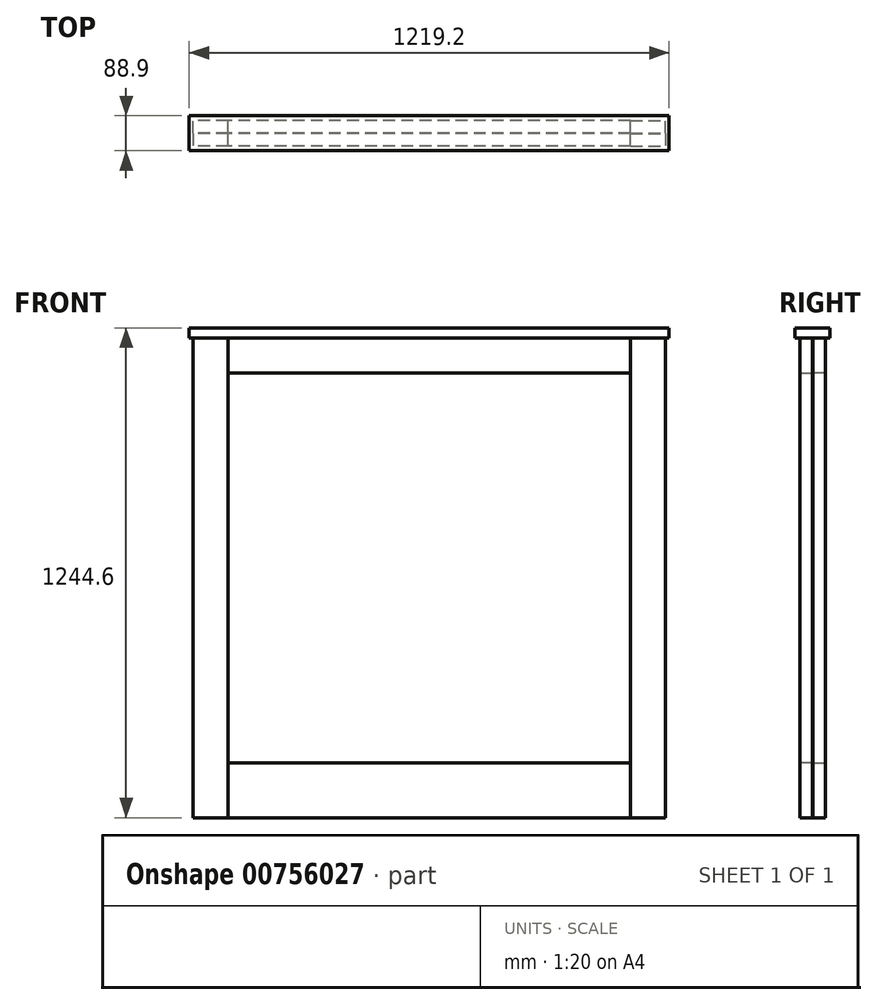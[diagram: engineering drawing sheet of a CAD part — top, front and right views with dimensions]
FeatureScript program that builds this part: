
annotation { "Feature Type Name" : "Feature", "Feature Type Description" : "" }
export const myFeature = defineFeature(function(context is Context, id is Id, definition is map)
    precondition{}
    {
        {
            var Q0;
            Q0=qCreatedBy(makeId("Top.planeOp"),FACE);
            var sketch = newSketch(context, id + "F0", { "sketchPlane" : qUnion([Q0])});
            skLineSegment(sketch, "E0.bottom", {"start": v(511.18, -0.8) * mm, "end": v(600.08, -0.8) * mm});
            skLineSegment(sketch, "E0.top", {"start": v(511.18, -32.54) * mm, "end": v(600.08, -32.54) * mm});
            skLineSegment(sketch, "E0.left", {"start": v(511.18, -0.8) * mm, "end": v(511.18, -32.54) * mm});
            skLineSegment(sketch, "E0.right", {"start": v(600.08, -0.8) * mm, "end": v(600.08, -32.54) * mm});
            skLineSegment(sketch, "E1.bottom", {"start": v(-511.18, -0.8) * mm, "end": v(-600.08, -0.8) * mm});
            skLineSegment(sketch, "E1.top", {"start": v(-511.18, -32.54) * mm, "end": v(-600.08, -32.54) * mm});
            skLineSegment(sketch, "E1.left", {"start": v(-511.18, -0.8) * mm, "end": v(-511.18, -32.54) * mm});
            skLineSegment(sketch, "E1.right", {"start": v(-600.08, -0.8) * mm, "end": v(-600.08, -32.54) * mm});
            skSolve(sketch);
        }
        {
            var Q0;
            Q0=makeQuery(id+"F0.imprint","IMPRINT",FACE,{"disambiguationData":[TD([[makeQuery(id+"F0.imprint","IMPRINT",EDGE,{"derivedFrom":sQuery(id+"F0.wireOp",EDGE,"E1.bottom")}),1.0]])]});
            var Q1;
            Q1=makeQuery(id+"F0.imprint","IMPRINT",FACE,{"disambiguationData":[TD([[makeQuery(id+"F0.imprint","IMPRINT",EDGE,{"derivedFrom":sQuery(id+"F0.wireOp",EDGE,"E0.bottom")}),-1.0]])]});
            extrude(context, id + "F1", {"entities" : qUnion([Q0, Q1]), "depth" : 1219.2 * mm, "offsetDistance" : 25.4 * mm});
        }
        {
            var Q0;
            Q0=qCreatedBy(makeId("Right.planeOp"),FACE);
            var sketch = newSketch(context, id + "F2", { "sketchPlane" : qUnion([Q0])});
            skLineSegment(sketch, "E2.bottom", {"start": v(-32.54, 1219.2) * mm, "end": v(-0.8, 1219.2) * mm});
            skLineSegment(sketch, "E2.top", {"start": v(-32.54, 1130.3) * mm, "end": v(-0.8, 1130.3) * mm});
            skLineSegment(sketch, "E2.left", {"start": v(-32.54, 1219.2) * mm, "end": v(-32.54, 1130.3) * mm});
            skLineSegment(sketch, "E2.right", {"start": v(-0.8, 1219.2) * mm, "end": v(-0.8, 1130.3) * mm});
            skLineSegment(sketch, "E3.bottom", {"start": v(-0.8, 139.7) * mm, "end": v(-32.54, 139.7) * mm});
            skLineSegment(sketch, "E3.top", {"start": v(-0.8, 0) * mm, "end": v(-32.54, 0) * mm});
            skLineSegment(sketch, "E3.left", {"start": v(-0.8, 139.7) * mm, "end": v(-0.8, 0) * mm});
            skLineSegment(sketch, "E3.right", {"start": v(-32.54, 139.7) * mm, "end": v(-32.54, 0) * mm});
            skPoint(sketch, "E4.oppositeSnap0", {"position": v(-16.67, 0) * mm});
            skSolve(sketch);
        }
        {
            var Q0;
            Q0=makeQuery(id+"F2.imprint","IMPRINT",FACE,{"disambiguationData":[TD([[makeQuery(id+"F2.imprint","IMPRINT",EDGE,{"derivedFrom":sQuery(id+"F2.wireOp",EDGE,"E3.bottom")}),1.0]])]});
            var Q1;
            Q1=makeQuery(id+"F2.imprint","IMPRINT",FACE,{"disambiguationData":[TD([[makeQuery(id+"F2.imprint","IMPRINT",EDGE,{"derivedFrom":sQuery(id+"F2.wireOp",EDGE,"E2.bottom")}),-1.0]])]});
            var Q2;
            Q2=makeQuery(id+"F1.opExtrude","SWEPT_FACE",FACE,{"disambiguationData":[OSD([sQuery(id+"F0.wireOp",EDGE,"E0.left")])]});
            var Q3;
            Q3=makeQuery(id+"F1.opExtrude","SWEPT_FACE",FACE,{"disambiguationData":[OSD([sQuery(id+"F0.wireOp",EDGE,"E1.left")])]});
            extrude(context, id + "F3", {"entities" : qUnion([Q0, Q1]), "endBound" : BoundingType.UP_TO_SURFACE, "depth" : 25.4 * mm, "endBoundEntityFace" : qUnion([Q2]), "offsetDistance" : 25.4 * mm, "hasSecondDirection" : true, "secondDirectionBound" : SecondDirectionBoundingType.UP_TO_SURFACE, "secondDirectionOppositeDirection" : true, "secondDirectionDepth" : 25.4 * mm, "secondDirectionBoundEntityFace" : qUnion([Q3])});
        }
        {
            var Q0;
            Q0=makeQuery(id+"F1.opExtrude","SWEPT_BODY",BODY,{"disambiguationData":[OSD([sQuery(id+"F0.wireOp",EDGE,"E0.bottom"),sQuery(id+"F0.wireOp",EDGE,"E0.top"),sQuery(id+"F0.wireOp",EDGE,"E0.left"),sQuery(id+"F0.wireOp",EDGE,"E0.right")])]});
            var Q1;
            Q1=makeQuery(id+"F3.opExtrude","SWEPT_BODY",BODY,{"disambiguationData":[OSD([sQuery(id+"F2.wireOp",EDGE,"E3.bottom"),sQuery(id+"F2.wireOp",EDGE,"E3.top"),sQuery(id+"F2.wireOp",EDGE,"E3.left"),sQuery(id+"F2.wireOp",EDGE,"E3.right")])]});
            var Q2;
            Q2=makeQuery(id+"F3.opExtrude","SWEPT_BODY",BODY,{"disambiguationData":[OSD([sQuery(id+"F2.wireOp",EDGE,"E2.bottom"),sQuery(id+"F2.wireOp",EDGE,"E2.top"),sQuery(id+"F2.wireOp",EDGE,"E2.left"),sQuery(id+"F2.wireOp",EDGE,"E2.right")])]});
            var Q3;
            Q3=makeQuery(id+"F1.opExtrude","SWEPT_BODY",BODY,{"disambiguationData":[OSD([sQuery(id+"F0.wireOp",EDGE,"E1.bottom"),sQuery(id+"F0.wireOp",EDGE,"E1.top"),sQuery(id+"F0.wireOp",EDGE,"E1.left"),sQuery(id+"F0.wireOp",EDGE,"E1.right")])]});
            var Q4;
            Q4=qCreatedBy(makeId("Front.planeOp"),FACE);
            mirror(context, id + "F4", {"entities" : qUnion([Q0, Q1, Q2, Q3]), "mirrorPlane" : qUnion([Q4])});
        }
        {
            var Q0;
            Q0=qCreatedBy(makeId("Right.planeOp"),FACE);
            var sketch = newSketch(context, id + "F5", { "sketchPlane" : qUnion([Q0])});
            skLineSegment(sketch, "E5.bottom", {"start": v(-44.45, 1244.6) * mm, "end": v(44.45, 1244.6) * mm});
            skLineSegment(sketch, "E5.top", {"start": v(-44.45, 1219.2) * mm, "end": v(44.45, 1219.2) * mm});
            skLineSegment(sketch, "E5.left", {"start": v(-44.45, 1244.6) * mm, "end": v(-44.45, 1219.2) * mm});
            skLineSegment(sketch, "E5.right", {"start": v(44.45, 1244.6) * mm, "end": v(44.45, 1219.2) * mm});
            skSolve(sketch);
        }
        {
            var Q0;
            Q0=makeQuery(id+"F5.imprint","IMPRINT",FACE,{"disambiguationData":[TD([[makeQuery(id+"F5.imprint","IMPRINT",EDGE,{"derivedFrom":sQuery(id+"F5.wireOp",EDGE,"E5.bottom")}),-1.0]])]});
            extrude(context, id + "F6", {"entities" : qUnion([Q0]), "endBound" : BoundingType.SYMMETRIC, "depth" : 1219.2 * mm, "offsetDistance" : 25.4 * mm});
        }
    });
